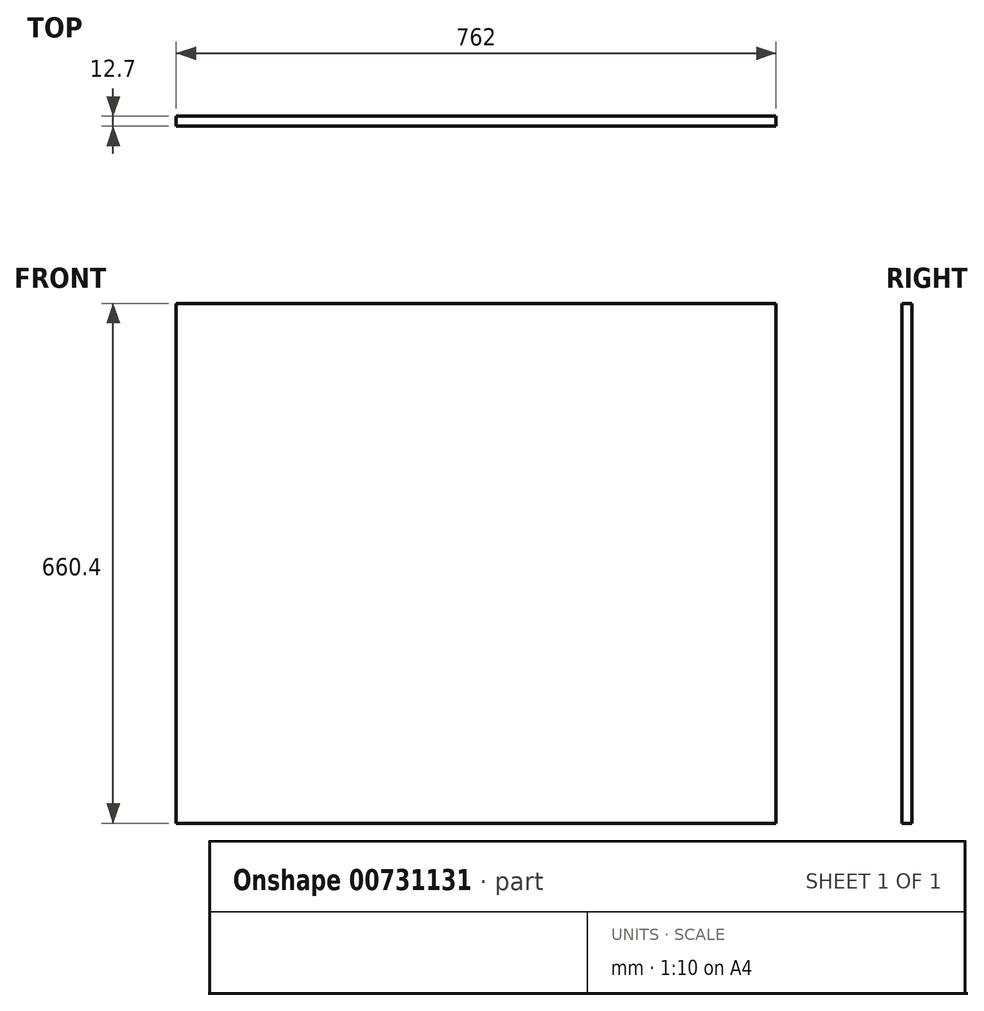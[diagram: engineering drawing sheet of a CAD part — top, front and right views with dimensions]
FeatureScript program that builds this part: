
annotation { "Feature Type Name" : "Feature", "Feature Type Description" : "" }
export const myFeature = defineFeature(function(context is Context, id is Id, definition is map)
    precondition{}
    {
        {
            var Q0;
            Q0=qCreatedBy(makeId("Front.planeOp"),FACE);
            var sketch = newSketch(context, id + "F0", { "sketchPlane" : qUnion([Q0])});
            skLineSegment(sketch, "E0.bottom", {"start": v(381, 333.99) * mm, "end": v(-381, 333.99) * mm});
            skLineSegment(sketch, "E0.top", {"start": v(381, -326.41) * mm, "end": v(-381, -326.41) * mm});
            skLineSegment(sketch, "E0.left", {"start": v(381, 333.99) * mm, "end": v(381, -326.41) * mm});
            skLineSegment(sketch, "E0.right", {"start": v(-381, 333.99) * mm, "end": v(-381, -326.41) * mm});
            skPoint(sketch, "E0.middle", {"position": v(0, 3.79) * mm});
            skSolve(sketch);
        }
        {
            var Q0;
            Q0 = qSketchRegion(id + "F0", true);
            extrude(context, id + "F1", {"entities" : qUnion([Q0]), "depth" : 12.7 * mm, "offsetDistance" : 25.4 * mm});
        }
    });
